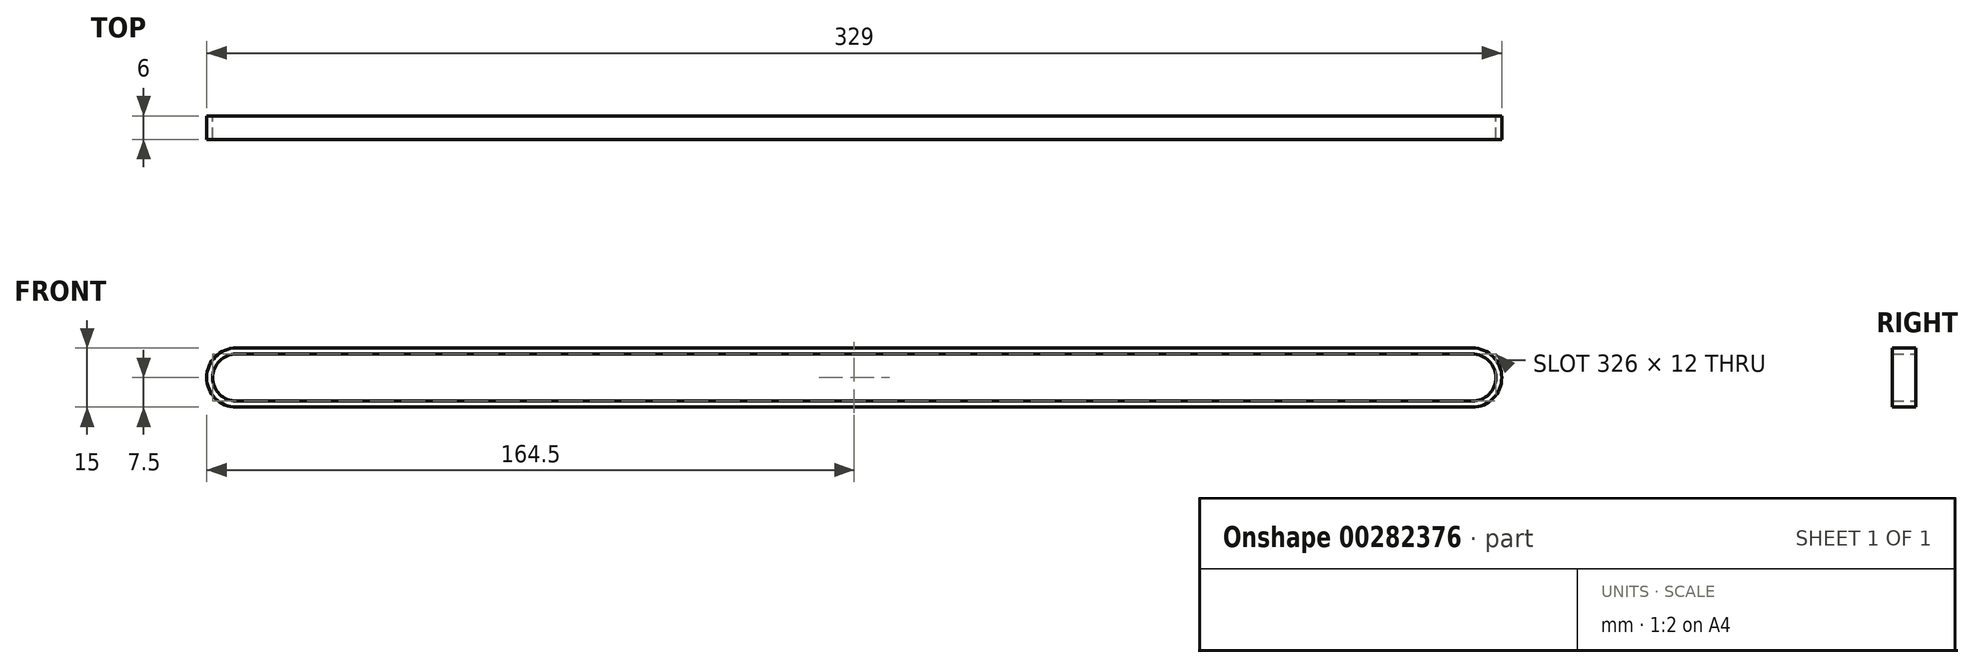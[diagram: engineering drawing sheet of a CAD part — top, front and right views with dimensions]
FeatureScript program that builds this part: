
annotation { "Feature Type Name" : "Feature", "Feature Type Description" : "" }
export const myFeature = defineFeature(function(context is Context, id is Id, definition is map)
    precondition{}
    {
        {
            var Q0;
            Q0=qCreatedBy(makeId("Front.planeOp"),FACE);
            var sketch = newSketch(context, id + "F0", { "sketchPlane" : qUnion([Q0])});
            skArc(sketch, "E0", {"start": v(0, 6) * mm, "mid": v(-6, 0) * mm, "end": v(0, -6) * mm});
            skArc(sketch, "E1", {"start": v(0, 7.5) * mm, "mid": v(-7.5, 0) * mm, "end": v(0, -7.5) * mm});
            skLineSegment(sketch, "E2", {"start": v(0, 0) * mm, "end": v(314, 0) * mm, "construction": true});
            skArc(sketch, "E3", {"start": v(314, -6) * mm, "mid": v(320, 0) * mm, "end": v(314, 6) * mm});
            skArc(sketch, "E4", {"start": v(314, -7.5) * mm, "mid": v(321.5, 0) * mm, "end": v(314, 7.5) * mm});
            skLineSegment(sketch, "E5", {"start": v(0, -7.5) * mm, "end": v(314, -7.5) * mm});
            skLineSegment(sketch, "E6", {"start": v(314, -6) * mm, "end": v(0, -6) * mm});
            skLineSegment(sketch, "E7", {"start": v(0, 6) * mm, "end": v(314, 6) * mm});
            skLineSegment(sketch, "E8", {"start": v(314, 7.5) * mm, "end": v(0, 7.5) * mm});
            skSolve(sketch);
        }
        {
            var Q0;
            Q0=qSketchRegion(id+"F0",true);
            extrude(context, id + "F1", {"entities" : qUnion([Q0]), "depth" : 6 * mm});
        }
    });
